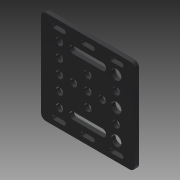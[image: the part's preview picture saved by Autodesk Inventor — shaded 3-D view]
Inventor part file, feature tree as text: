
AUTODESK INVENTOR PART (.ipt)
format: ipt  version: 2014 SP1 (Build 180222100, 222)  size: 229,888 bytes
history: native  units: in
note: dims shown in document units (in); Inventor stores cm internally (conversion verified against a paired STEP export)
features: extrude x3, sketch x3, fillet x1
ambient origin geometry x8: Origin, YZ Plane, XZ Plane, XY Plane, X Axis, Y Axis, Z Axis, Center Point
bodies: Solid1 (feature_tree)
feature tree (7):
  extrude  "Extrusion1"  Depth=2.5787in
  extrude  "Extrusion2"  Depth=0.1969in
  extrude  "Extrusion3"  Depth=0.3937in
  fillet  "Fillet1"  Radius=1.5748in
  sketch  "Sketch1"  dims[d0=2.5787in d1=2.5787in]
  sketch  "Sketch2"  dims[d2=0.1181in d3=0.0in d4=0.1969in]
  sketch  "Sketch3"  dims[d5=0.1969in d6=0.3937in d7=1.5748in d9=360.0deg d11=0.1969in d12=0.5079in d13=1.1811in d15=0.3937in d16=1.1811in d18=0.3937in d21=0.1969in d22=0.1969in d23=0.5079in d24=0.3937in d25=0.2835in d26=0.7874in d28=0.7874in d29=0.7874in d31=0.7874in d34=0.1181in d35=0.0in d36=0.1969in d37=0.8126in d38=0.1181in d39=2.3799in d40=0.2559in d41=0.7874in d43=0.7933in d44=0.7874in d46=0.7933in d49=0.1181in d50=0.0in d51=0.1331in]
